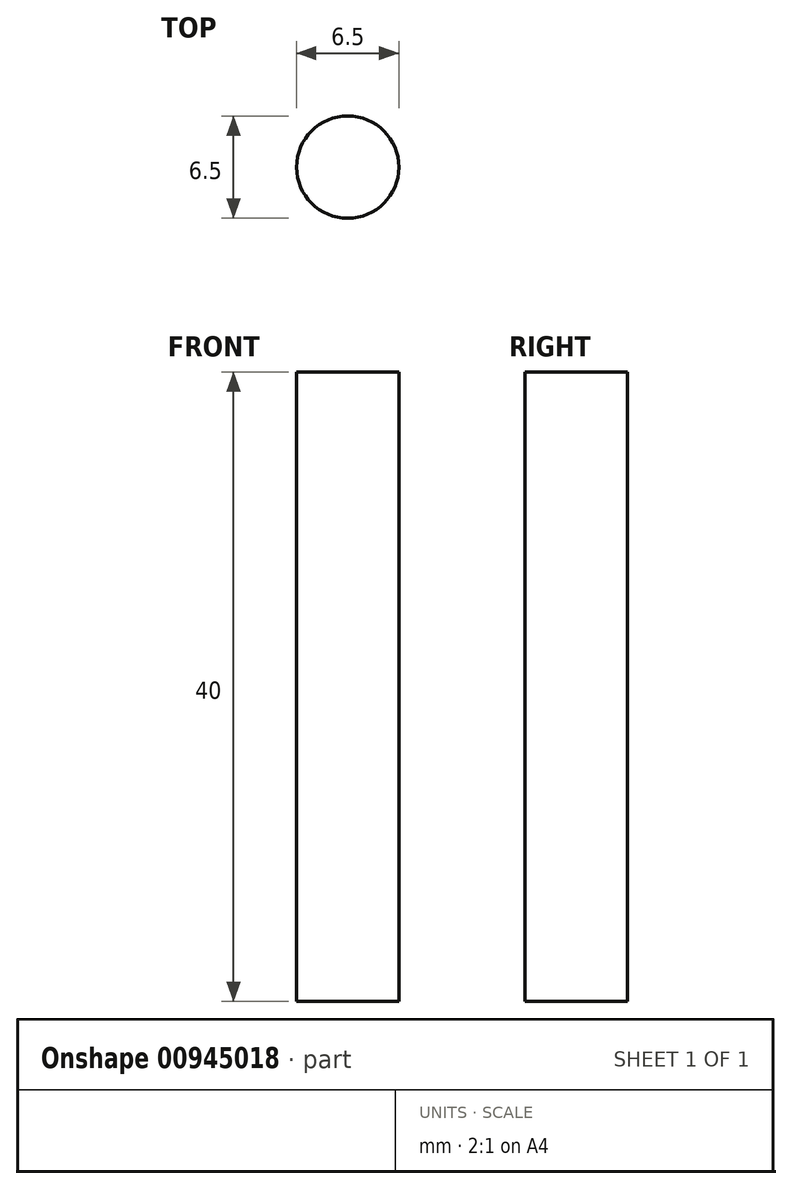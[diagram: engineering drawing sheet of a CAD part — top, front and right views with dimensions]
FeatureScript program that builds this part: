
annotation { "Feature Type Name" : "Feature", "Feature Type Description" : "" }
export const myFeature = defineFeature(function(context is Context, id is Id, definition is map)
    precondition{}
    {
        {
            var Q0;
            Q0=qCreatedBy(makeId("Top.planeOp"),FACE);
            var sketch = newSketch(context, id + "F0", { "sketchPlane" : qUnion([Q0])});
            skCircle(sketch, "E0", {"center": v(0, 0) * mm, "radius": 3.25 * mm});
            skSolve(sketch);
        }
        {
            var Q0;
            Q0 = qSketchRegion(id + "F0", true);
            extrude(context, id + "F1", {"entities" : qUnion([Q0]), "depth" : 40 * mm, "offsetDistance" : 25 * mm});
        }
    });
